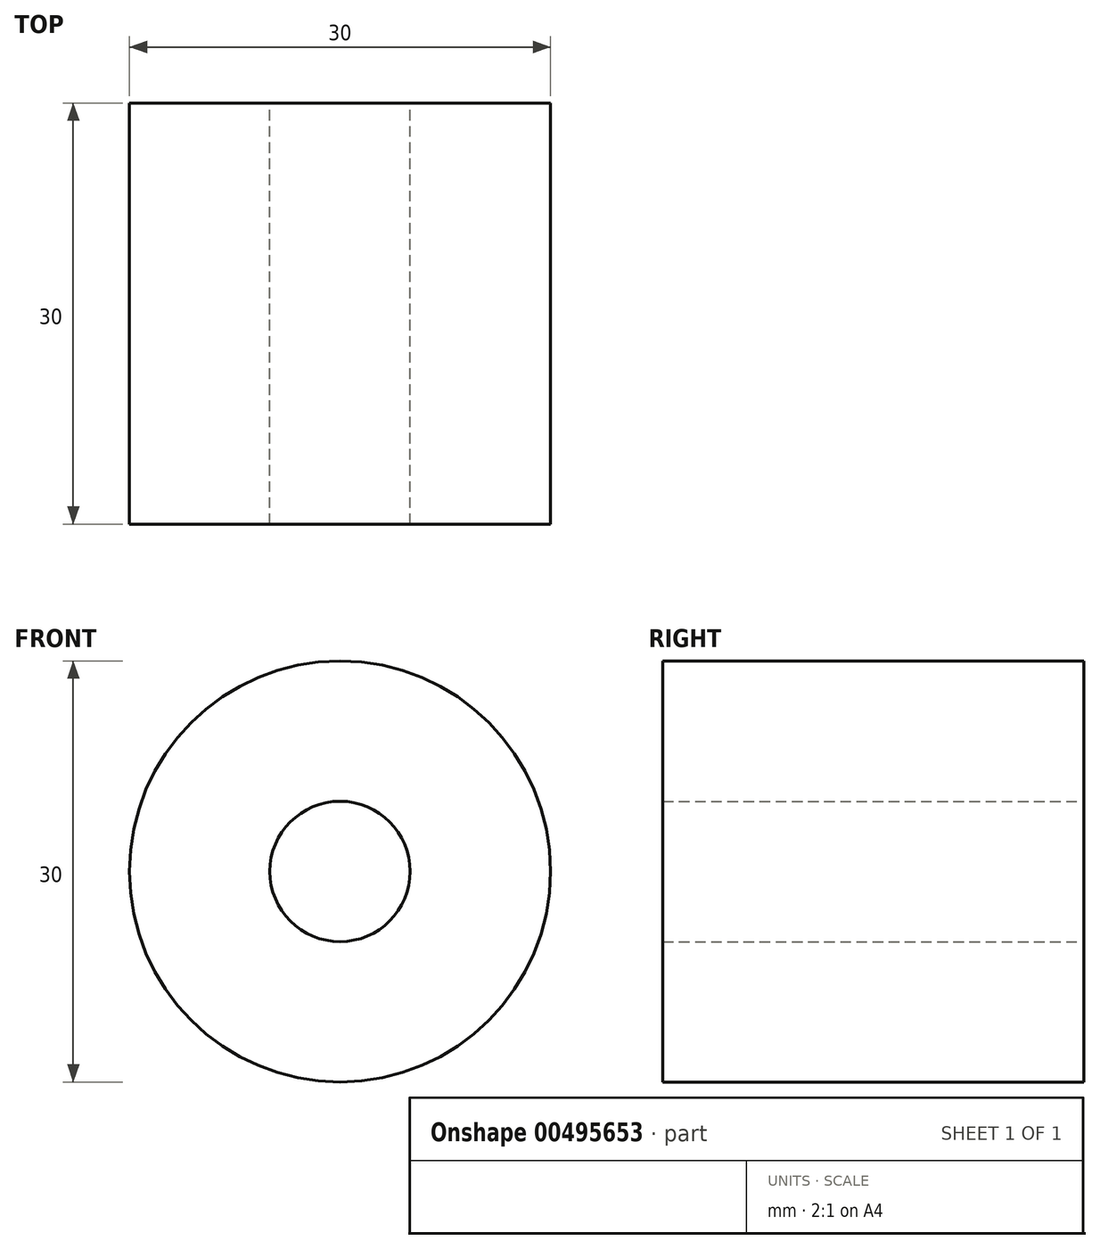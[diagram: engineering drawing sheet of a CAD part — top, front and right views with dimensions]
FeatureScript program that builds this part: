
annotation { "Feature Type Name" : "Feature", "Feature Type Description" : "" }
export const myFeature = defineFeature(function(context is Context, id is Id, definition is map)
    precondition{}
    {
        {
            var Q0;
            Q0=qCreatedBy(makeId("Front.planeOp"),FACE);
            var sketch = newSketch(context, id + "F0", { "sketchPlane" : qUnion([Q0])});
            skCircle(sketch, "E0", {"center": v(0, 0) * mm, "radius": 15 * mm});
            skCircle(sketch, "E1", {"center": v(0, 0) * mm, "radius": 5 * mm});
            skSolve(sketch);
        }
        {
            var Q0;
            Q0 = qSketchRegion(id + "F0", true);
            extrude(context, id + "F1", {"entities" : qUnion([Q0]), "depth" : 30 * mm, "offsetDistance" : 25 * mm});
        }
    });
